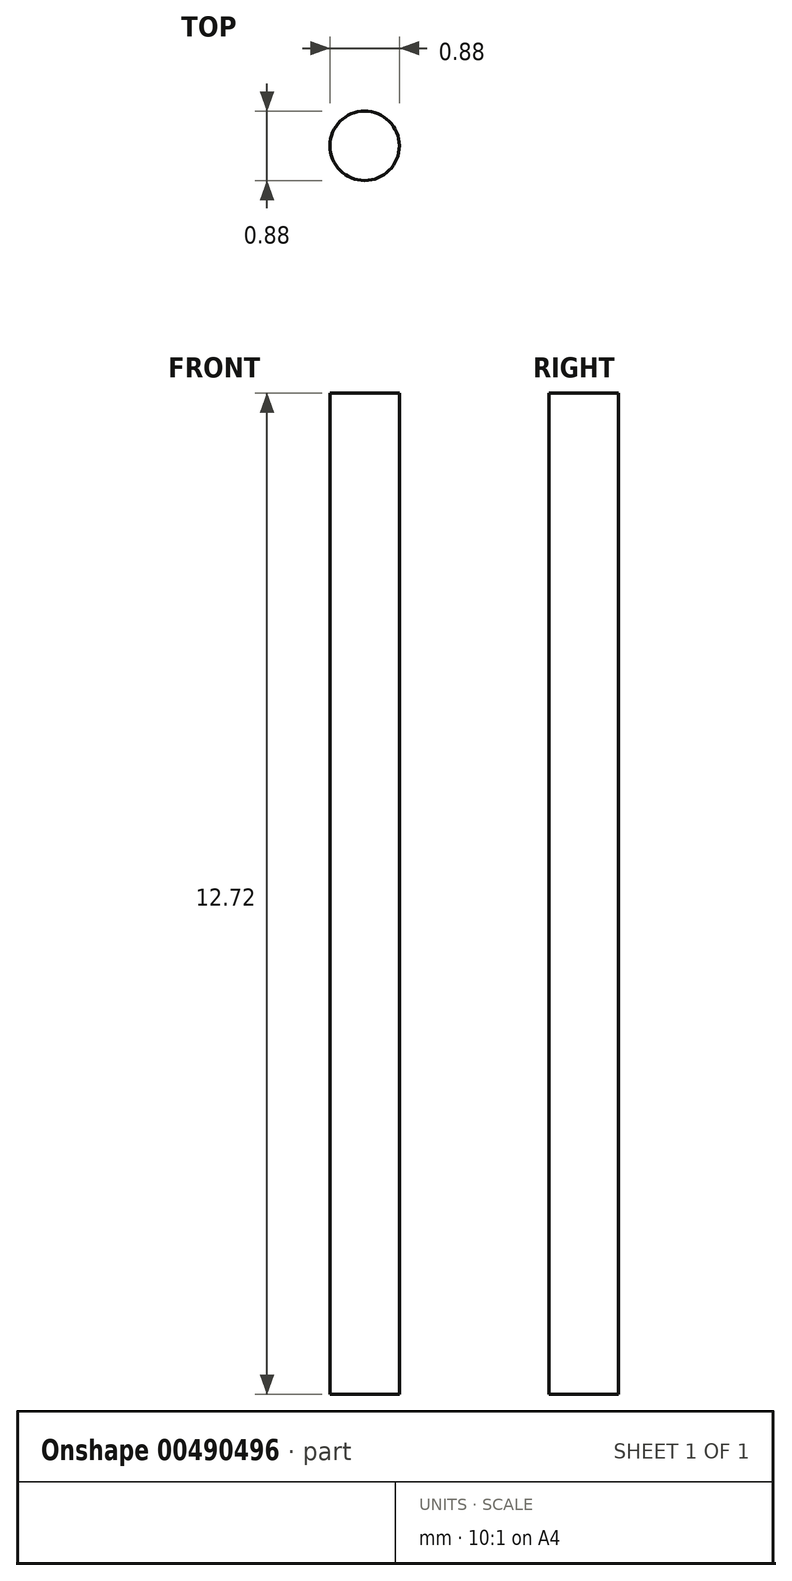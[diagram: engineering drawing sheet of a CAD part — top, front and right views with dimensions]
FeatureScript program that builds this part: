
annotation { "Feature Type Name" : "Feature", "Feature Type Description" : "" }
export const myFeature = defineFeature(function(context is Context, id is Id, definition is map)
    precondition{}
    {
        {
            var Q0;
            Q0=qCreatedBy(makeId("Top.planeOp"),FACE);
            var sketch = newSketch(context, id + "F0", { "sketchPlane" : qUnion([Q0])});
            skLineSegment(sketch, "E0", {"start": v(0, 0) * mm, "end": v(0, -27.09) * mm, "construction": true});
            skSolve(sketch);
        }
        {
            var Q0;
            Q0=qCreatedBy(makeId("Right.planeOp"),FACE);
            var sketch = newSketch(context, id + "F1", { "sketchPlane" : qUnion([Q0])});
            skLineSegment(sketch, "E1", {"start": v(0, 0) * mm, "end": v(0, -12.72) * mm, "construction": true});
            skLineSegment(sketch, "E2", {"start": v(-27.09, 0) * mm, "end": v(-27.09, -6.49) * mm, "construction": true});
            skLineSegment(sketch, "E3", {"start": v(-27.09, -6.49) * mm, "end": v(0, -12.72) * mm, "construction": true});
            skSolve(sketch);
        }
        {
            var Q0;
            Q0=qCreatedBy(makeId("Front.planeOp"),FACE);
            var sketch = newSketch(context, id + "F2", { "sketchPlane" : qUnion([Q0])});
            skCircle(sketch, "E4", {"center": v(0, 0) * mm, "radius": 0.44 * mm});
            skSolve(sketch);
        }
        {
            var Q0;
            Q0=makeQuery(id+"F2.imprint","IMPRINT",FACE,{"disambiguationData":[TD([[makeQuery(id+"F2.imprint","IMPRINT",EDGE,{"derivedFrom":sQuery(id+"F2.wireOp",EDGE,"E4")}),1.0]])]});
            var Q1;
            Q1=sQuery(id+"F2.wireOp",EDGE,"E4");
            extrude(context, id + "F3", {"entities" : qUnion([Q0]), "bodyType" : ToolBodyType.SURFACE, "surfaceEntities" : qUnion([Q1]), "depth" : 27.05 * mm, "offsetDistance" : 25.4 * mm});
        }
        {
            var Q0;
            Q0=qCreatedBy(makeId("Top.planeOp"),FACE);
            var sketch = newSketch(context, id + "F4", { "sketchPlane" : qUnion([Q0])});
            skCircle(sketch, "E5", {"center": v(0, 0) * mm, "radius": 0.44 * mm});
            skCircle(sketch, "E6", {"center": v(31.07, -166.25) * mm, "radius": 0.53 * mm});
            skCircle(sketch, "E7", {"center": v(0, -27.09) * mm, "radius": 0.44 * mm});
            skSolve(sketch);
        }
        {
            var Q0;
            Q0=makeQuery(id+"F4.imprint","IMPRINT",FACE,{"disambiguationData":[TD([[makeQuery(id+"F4.imprint","IMPRINT",EDGE,{"derivedFrom":sQuery(id+"F4.wireOp",EDGE,"E5")}),1.0]])]});
            var Q1;
            Q1=sQuery(id+"F1.wireOp",VERTEX,"E3.end");
            extrude(context, id + "F5", {"entities" : qUnion([Q0]), "endBound" : BoundingType.UP_TO_VERTEX, "oppositeDirection" : true, "depth" : 25.4 * mm, "endBoundEntityVertex" : qUnion([Q1]), "offsetDistance" : 25.4 * mm});
        }
        {
            var Q0;
            Q0=sQuery(id+"F4.wireOp",EDGE,"E7");
            var Q1;
            Q1=sQuery(id+"F1.wireOp",VERTEX,"E3.start");
            extrude(context, id + "F6", {"bodyType" : ToolBodyType.SURFACE, "surfaceEntities" : qUnion([Q0]), "endBound" : BoundingType.UP_TO_VERTEX, "oppositeDirection" : true, "depth" : 25.4 * mm, "endBoundEntityVertex" : qUnion([Q1]), "offsetDistance" : 25.4 * mm});
        }
        {
            var Q0;
            Q0=qCreatedBy(makeId("Front.planeOp"),FACE);
            var sketch = newSketch(context, id + "F7", { "sketchPlane" : qUnion([Q0])});
            skCircle(sketch, "E8", {"center": v(0, -12.72) * mm, "radius": 0.44 * mm});
            skSolve(sketch);
        }
        {
            var Q0;
            Q0 = qSketchRegion(id + "F7", true);
            var Q1;
            Q1=sQuery(id+"F7.wireOp",EDGE,"E8");
            var Q2;
            Q2=sQuery(id+"F1.wireOp",VERTEX,"E3.start");
            extrude(context, id + "F8", {"entities" : qUnion([Q0]), "bodyType" : ToolBodyType.SURFACE, "surfaceEntities" : qUnion([Q1]), "endBound" : BoundingType.UP_TO_VERTEX, "depth" : 25.4 * mm, "endBoundEntityVertex" : qUnion([Q2]), "offsetDistance" : 25.4 * mm});
        }
    });
